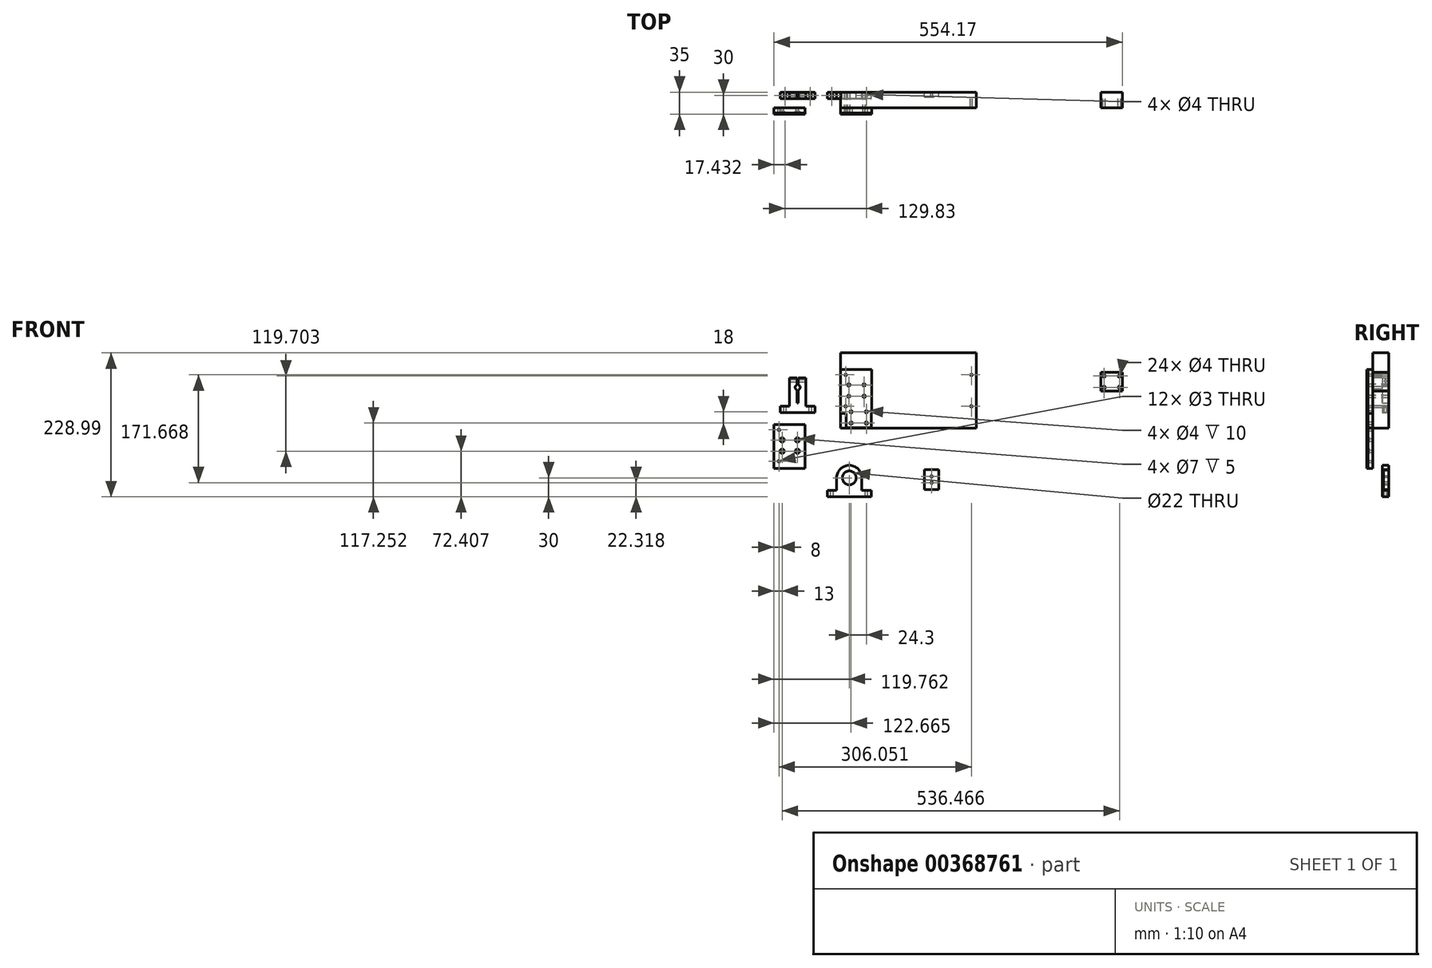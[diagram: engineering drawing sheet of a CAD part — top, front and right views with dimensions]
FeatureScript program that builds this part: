
annotation { "Feature Type Name" : "Feature", "Feature Type Description" : "" }
export const myFeature = defineFeature(function(context is Context, id is Id, definition is map)
    precondition{}
    {
        {
            var Q0;
            Q0=qCreatedBy(makeId("Front.planeOp"),FACE);
            var sketch = newSketch(context, id + "F0", { "sketchPlane" : qUnion([Q0])});
            skCircle(sketch, "E0", {"center": v(-230.1, -138.1) * mm, "radius": 11 * mm});
            skCircle(sketch, "E1", {"center": v(-230.1, -138.1) * mm, "radius": 4 * mm});
            skArc(sketch, "E2", {"start": v(-250.1, -138.1) * mm, "mid": v(-230.1, -118.1) * mm, "end": v(-210.1, -138.1) * mm});
            skLineSegment(sketch, "E3", {"start": v(-250.1, -138.1) * mm, "end": v(-250.1, -158.1) * mm});
            skLineSegment(sketch, "E4", {"start": v(-250.1, -158.1) * mm, "end": v(-265.1, -158.1) * mm});
            skLineSegment(sketch, "E5", {"start": v(-265.1, -158.1) * mm, "end": v(-265.1, -168.1) * mm});
            skLineSegment(sketch, "E6", {"start": v(-265.1, -168.1) * mm, "end": v(-195.1, -168.1) * mm});
            skLineSegment(sketch, "E7", {"start": v(-195.1, -168.1) * mm, "end": v(-195.1, -158.1) * mm});
            skLineSegment(sketch, "E8", {"start": v(-195.1, -158.1) * mm, "end": v(-210.1, -158.1) * mm});
            skLineSegment(sketch, "E9", {"start": v(-210.1, -158.1) * mm, "end": v(-210.1, -138.1) * mm});
            skLineSegment(sketch, "E10", {"start": v(-324.94, 21.01) * mm, "end": v(-324.94, -23.99) * mm});
            skLineSegment(sketch, "E11", {"start": v(-324.94, -23.99) * mm, "end": v(-339.94, -23.99) * mm});
            skLineSegment(sketch, "E12", {"start": v(-339.94, -23.99) * mm, "end": v(-339.94, -33.99) * mm});
            skLineSegment(sketch, "E13", {"start": v(-339.94, -33.99) * mm, "end": v(-284.44, -33.99) * mm});
            skLineSegment(sketch, "E14", {"start": v(-284.44, -33.99) * mm, "end": v(-284.44, -23.99) * mm});
            skLineSegment(sketch, "E15", {"start": v(-284.44, -23.99) * mm, "end": v(-299.44, -23.99) * mm});
            skLineSegment(sketch, "E16", {"start": v(-299.44, -23.99) * mm, "end": v(-299.44, 21.01) * mm});
            skPoint(sketch, "E17", {"position": v(-324.94, -1.49) * mm});
            skPoint(sketch, "E18", {"position": v(-312.19, -33.99) * mm});
            skLineSegment(sketch, "E19", {"start": v(-313.19, -18.99) * mm, "end": v(-311.19, -18.99) * mm});
            skLineSegment(sketch, "E20", {"start": v(-311.19, -18.99) * mm, "end": v(-311.19, 6.01) * mm});
            skLineSegment(sketch, "E21", {"start": v(-313.19, -18.99) * mm, "end": v(-313.19, 6.01) * mm});
            skPoint(sketch, "E22", {"position": v(-312.19, -18.99) * mm});
            skCircle(sketch, "E23", {"center": v(-312.19, 6.01) * mm, "radius": 4 * mm});
            skLineSegment(sketch, "E24", {"start": v(-324.94, 21.01) * mm, "end": v(-313.19, 21.01) * mm});
            skLineSegment(sketch, "E25", {"start": v(-313.19, 21.01) * mm, "end": v(-313.19, 6.01) * mm});
            skLineSegment(sketch, "E26", {"start": v(-311.19, 21.01) * mm, "end": v(-299.44, 21.01) * mm});
            skLineSegment(sketch, "E27", {"start": v(-311.19, 6.01) * mm, "end": v(-311.19, 21.01) * mm});
            skLineSegment(sketch, "E28.bottom", {"start": v(-110.58, -124.8) * mm, "end": v(-87.58, -124.8) * mm});
            skLineSegment(sketch, "E28.top", {"start": v(-110.58, -156.8) * mm, "end": v(-87.58, -156.8) * mm});
            skLineSegment(sketch, "E28.left", {"start": v(-110.58, -124.8) * mm, "end": v(-110.58, -156.8) * mm});
            skLineSegment(sketch, "E28.right", {"start": v(-87.58, -124.8) * mm, "end": v(-87.58, -156.8) * mm});
            skPoint(sketch, "E29", {"position": v(-99.08, -124.8) * mm});
            skCircle(sketch, "E30", {"center": v(-99.08, -135.8) * mm, "radius": 1.5 * mm});
            skCircle(sketch, "E31", {"center": v(-99.08, -145.8) * mm, "radius": 1.5 * mm});
            skSolve(sketch);
        }
        {
            var Q0;
            Q0=makeQuery(id+"F0.imprint","IMPRINT",FACE,{"disambiguationData":[TD([[makeQuery(id+"F0.imprint","IMPRINT",EDGE,{"derivedFrom":sQuery(id+"F0.wireOp",EDGE,"E0")}),-1.0]])]});
            extrude(context, id + "F1", {"entities" : qUnion([Q0]), "depth" : 10 * mm, "offsetDistance" : 25 * mm});
        }
        {
            var Q0;
            Q0=makeQuery(id+"F1.opExtrude","SWEPT_FACE",FACE,{"disambiguationData":[OSD([sQuery(id+"F0.wireOp",EDGE,"E4")])]});
            var sketch = newSketch(context, id + "F2", { "sketchPlane" : qUnion([Q0])});
            skCircle(sketch, "E32", {"center": v(-257.6, -5) * mm, "radius": 2 * mm});
            skCircle(sketch, "E33", {"center": v(-202.6, -5) * mm, "radius": 2 * mm});
            skPoint(sketch, "E33.centerSnap0", {"position": v(-250.1, -5) * mm});
            skPoint(sketch, "E34", {"position": v(-265.1, -5) * mm});
            skSolve(sketch);
        }
        {
            var Q0;
            Q0 = qSketchRegion(id + "F2", true);
            extrude(context, id + "F3", {"entities" : qUnion([Q0]), "operationType" : NewBodyOperationType.REMOVE, "oppositeDirection" : true, "depth" : 25 * mm, "offsetDistance" : 25 * mm});
        }
        {
            var Q0;
            Q0=makeQuery(id+"F0.imprint","IMPRINT",FACE,{"disambiguationData":[TD([[makeQuery(id+"F0.imprint","IMPRINT",EDGE,{"derivedFrom":sQuery(id+"F0.wireOp",EDGE,"E10")}),1.0]])]});
            extrude(context, id + "F4", {"entities" : qUnion([Q0]), "depth" : 10 * mm, "offsetDistance" : 25 * mm});
        }
        {
            var Q0;
            Q0=makeQuery(id+"F4.opExtrude","SWEPT_FACE",FACE,{"disambiguationData":[OSD([sQuery(id+"F0.wireOp",EDGE,"E10")])]});
            var sketch = newSketch(context, id + "F5", { "sketchPlane" : qUnion([Q0])});
            skCircle(sketch, "E35", {"center": v(4.76, 16.01) * mm, "radius": 2 * mm});
            skSolve(sketch);
        }
        {
            var Q0;
            Q0=makeQuery(id+"F5.imprint","IMPRINT",FACE,{"disambiguationData":[TD([[makeQuery(id+"F5.imprint","IMPRINT",EDGE,{"derivedFrom":sQuery(id+"F5.wireOp",EDGE,"E35")}),1.0]])]});
            extrude(context, id + "F6", {"entities" : qUnion([Q0]), "operationType" : NewBodyOperationType.REMOVE, "oppositeDirection" : true, "depth" : 36.2 * mm, "offsetDistance" : 25 * mm});
        }
        {
            var Q0;
            Q0=makeQuery(id+"F4.opExtrude","SWEPT_FACE",FACE,{"disambiguationData":[OSD([sQuery(id+"F0.wireOp",EDGE,"E11")])]});
            var sketch = newSketch(context, id + "F7", { "sketchPlane" : qUnion([Q0])});
            skCircle(sketch, "E36", {"center": v(-332.44, -5) * mm, "radius": 2 * mm});
            skPoint(sketch, "E37", {"position": v(-332.44, 0) * mm});
            skPoint(sketch, "E38", {"position": v(-339.94, -5) * mm});
            skSolve(sketch);
        }
        {
            var Q0;
            Q0=makeQuery(id+"F4.opExtrude","SWEPT_FACE",FACE,{"disambiguationData":[OSD([sQuery(id+"F0.wireOp",EDGE,"E15")])]});
            var sketch = newSketch(context, id + "F8", { "sketchPlane" : qUnion([Q0])});
            skPoint(sketch, "E39", {"position": v(-291.94, 0) * mm});
            skPoint(sketch, "E40", {"position": v(-284.44, -5) * mm});
            skCircle(sketch, "E41", {"center": v(-291.94, -5) * mm, "radius": 2 * mm});
            skSolve(sketch);
        }
        {
            var Q0;
            Q0=makeQuery(id+"F8.imprint","IMPRINT",FACE,{"disambiguationData":[TD([[makeQuery(id+"F8.imprint","IMPRINT",EDGE,{"derivedFrom":sQuery(id+"F8.wireOp",EDGE,"E41")}),1.0]])]});
            var Q1;
            Q1=makeQuery(id+"F7.imprint","IMPRINT",FACE,{"disambiguationData":[TD([[makeQuery(id+"F7.imprint","IMPRINT",EDGE,{"derivedFrom":sQuery(id+"F7.wireOp",EDGE,"E36")}),1.0]])]});
            var Q2;
            Q2 = qSketchRegion(id + "F10", true);
            extrude(context, id + "F9", {"entities" : qUnion([Q0, Q1, Q2]), "operationType" : NewBodyOperationType.REMOVE, "oppositeDirection" : true, "depth" : 25 * mm, "offsetDistance" : 25 * mm});
        }
        {
            var Q0;
            Q0=qCreatedBy(makeId("Front.planeOp"),FACE);
            var sketch = newSketch(context, id + "F10", { "sketchPlane" : qUnion([Q0])});
            skLineSegment(sketch, "E42.bottom", {"start": v(-243.82, 60.88) * mm, "end": v(-27.82, 60.88) * mm});
            skLineSegment(sketch, "E42.top", {"start": v(-243.82, -59.12) * mm, "end": v(-27.82, -59.12) * mm});
            skLineSegment(sketch, "E42.left", {"start": v(-243.82, 60.88) * mm, "end": v(-243.82, -59.12) * mm});
            skLineSegment(sketch, "E42.right", {"start": v(-27.82, 60.88) * mm, "end": v(-27.82, -59.12) * mm});
            skLineSegment(sketch, "E43", {"start": v(-235.82, 75.54) * mm, "end": v(-235.82, -77.95) * mm, "construction": true});
            skLineSegment(sketch, "E44", {"start": v(-35.82, 74.3) * mm, "end": v(-35.82, -77.95) * mm, "construction": true});
            skLineSegment(sketch, "E45", {"start": v(-230.82, 76.77) * mm, "end": v(-230.82, -80.82) * mm, "construction": true});
            skLineSegment(sketch, "E46", {"start": v(-40.82, 75.13) * mm, "end": v(-40.82, -75.08) * mm, "construction": true});
            skLineSegment(sketch, "E47", {"start": v(-274.06, -24.12) * mm, "end": v(20.6, -24.12) * mm, "construction": true});
            skLineSegment(sketch, "E48", {"start": v(-271.18, 25.88) * mm, "end": v(19.79, 25.88) * mm, "construction": true});
            skCircle(sketch, "E49", {"center": v(-235.82, 25.88) * mm, "radius": 1.5 * mm});
            skCircle(sketch, "E50", {"center": v(-235.82, -24.12) * mm, "radius": 1.5 * mm});
            skCircle(sketch, "E51", {"center": v(-35.82, 25.88) * mm, "radius": 1.5 * mm});
            skCircle(sketch, "E52", {"center": v(-35.82, -24.12) * mm, "radius": 1.5 * mm});
            skCircle(sketch, "E53", {"center": v(175.3, 24) * mm, "radius": 2 * mm});
            skCircle(sketch, "E54", {"center": v(175.3, 6) * mm, "radius": 2 * mm});
            skLineSegment(sketch, "E55.bottom", {"start": v(170.3, 30) * mm, "end": v(204.3, 30) * mm});
            skLineSegment(sketch, "E55.top", {"start": v(170.3, 0) * mm, "end": v(204.3, 0) * mm});
            skLineSegment(sketch, "E55.left", {"start": v(170.3, 30) * mm, "end": v(170.3, 0) * mm});
            skLineSegment(sketch, "E55.right", {"start": v(204.3, 30) * mm, "end": v(204.3, 0) * mm});
            skLineSegment(sketch, "E56", {"start": v(180.3, 30) * mm, "end": v(180.3, 0) * mm});
            skLineSegment(sketch, "E57", {"start": v(194.3, 30) * mm, "end": v(194.3, 0) * mm});
            skCircle(sketch, "E58", {"center": v(199.6, 24) * mm, "radius": 2 * mm});
            skCircle(sketch, "E59", {"center": v(199.6, 6) * mm, "radius": 2 * mm});
            skPoint(sketch, "E60", {"position": v(-243.82, 0.88) * mm});
            skPoint(sketch, "E61", {"position": v(170.3, 15) * mm});
            skCircle(sketch, "E62", {"center": v(-230.82, 9.88) * mm, "radius": 2 * mm});
            skCircle(sketch, "E63", {"center": v(-230.82, -8.12) * mm, "radius": 2 * mm});
            skLineSegment(sketch, "E64.bottom", {"start": v(-235.82, 15.88) * mm, "end": v(-201.82, 15.88) * mm});
            skLineSegment(sketch, "E64.top", {"start": v(-235.82, -14.12) * mm, "end": v(-201.82, -14.12) * mm});
            skLineSegment(sketch, "E64.left", {"start": v(-235.82, 15.88) * mm, "end": v(-235.82, -14.12) * mm});
            skLineSegment(sketch, "E64.right", {"start": v(-201.82, 15.88) * mm, "end": v(-201.82, -14.12) * mm});
            skLineSegment(sketch, "E65", {"start": v(-225.82, 15.88) * mm, "end": v(-225.82, -14.12) * mm});
            skLineSegment(sketch, "E66", {"start": v(-211.82, 15.88) * mm, "end": v(-211.82, -14.12) * mm});
            skCircle(sketch, "E67", {"center": v(-206.52, 9.88) * mm, "radius": 2 * mm});
            skCircle(sketch, "E68", {"center": v(-206.52, -8.12) * mm, "radius": 2 * mm});
            skPoint(sketch, "E69", {"position": v(-235.82, 0.88) * mm});
            skSolve(sketch);
        }
        {
            var Q0;
            Q0=makeQuery(id+"F10.imprint","IMPRINT",FACE,{"disambiguationData":[TD([[makeQuery(id+"F10.imprint","IMPRINT",EDGE,{"derivedFrom":sQuery(id+"F10.wireOp",EDGE,"E53")}),-1.0]])]});
            var Q1;
            {var subQ1=sQuery(id+"F10.wireOp",EDGE,"E55.right");Q1=makeQuery(id+"F10.imprint","IMPRINT",FACE,{"disambiguationData":[TD([[makeQuery(id+"F10.imprint","IMPRINT",EDGE,{"derivedFrom":subQ1}),-1.0]])]});}
            var Q2;
            Q2=makeQuery(id+"F10.imprint","IMPRINT",FACE,{"disambiguationData":[TD([[makeQuery(id+"F10.imprint","IMPRINT",EDGE,{"derivedFrom":sQuery(id+"F10.wireOp",EDGE,"E42.bottom")}),-1.0]])]});
            var Q3;
            {var subQ0=sQuery(id+"F10.wireOp",EDGE,"E56");Q3=makeQuery(id+"F10.imprint","IMPRINT",FACE,{"disambiguationData":[TD([[makeQuery(id+"F10.imprint","IMPRINT",EDGE,{"derivedFrom":subQ0}),1.0]])]});}
            var Q4;
            Q4=makeQuery(id+"F10.imprint","IMPRINT",FACE,{"disambiguationData":[TD([[makeQuery(id+"F10.imprint","IMPRINT",EDGE,{"derivedFrom":sQuery(id+"F10.wireOp",EDGE,"E62")}),-1.0]])]});
            var Q5;
            {var subQ0=sQuery(id+"F10.wireOp",EDGE,"E65");Q5=makeQuery(id+"F10.imprint","IMPRINT",FACE,{"disambiguationData":[TD([[makeQuery(id+"F10.imprint","IMPRINT",EDGE,{"derivedFrom":subQ0}),1.0]])]});}
            var Q6;
            {var subQ1=sQuery(id+"F10.wireOp",EDGE,"E64.right");Q6=makeQuery(id+"F10.imprint","IMPRINT",FACE,{"disambiguationData":[TD([[makeQuery(id+"F10.imprint","IMPRINT",EDGE,{"derivedFrom":subQ1}),-1.0]])]});}
            extrude(context, id + "F11", {"entities" : qUnion([Q0, Q1, Q2, Q3, Q4, Q5, Q6]), "depth" : 25 * mm, "offsetDistance" : 25 * mm});
        }
        {
            var Q0;
            Q0=makeQuery(id+"F11.opExtrude","CAP_FACE",FACE,{"disambiguationData":[OSD([sQuery(id+"F10.wireOp",EDGE,"E42.bottom"),sQuery(id+"F10.wireOp",EDGE,"E42.top"),sQuery(id+"F10.wireOp",EDGE,"E42.left"),sQuery(id+"F10.wireOp",EDGE,"E42.right"),sQuery(id+"F10.wireOp",EDGE,"E49"),sQuery(id+"F10.wireOp",EDGE,"E50"),sQuery(id+"F10.wireOp",EDGE,"E51"),sQuery(id+"F10.wireOp",EDGE,"E52"),sQuery(id+"F10.wireOp",EDGE,"E62"),sQuery(id+"F10.wireOp",EDGE,"E63"),sQuery(id+"F10.wireOp",EDGE,"E67"),sQuery(id+"F10.wireOp",EDGE,"E68")])],"isStart":false});
            var sketch = newSketch(context, id + "F12", { "sketchPlane" : qUnion([Q0])});
            skLineSegment(sketch, "E70.bottom", {"start": v(-194.52, 34.38) * mm, "end": v(-243.82, 34.38) * mm});
            skLineSegment(sketch, "E70.top", {"start": v(-194.52, -35.62) * mm, "end": v(-243.82, -35.62) * mm});
            skLineSegment(sketch, "E70.left", {"start": v(-194.52, 34.38) * mm, "end": v(-194.52, -35.62) * mm});
            skLineSegment(sketch, "E70.right", {"start": v(-243.82, 34.38) * mm, "end": v(-243.82, -35.62) * mm});
            skCircle(sketch, "E71", {"center": v(-206.52, 9.88) * mm, "radius": 2 * mm});
            skCircle(sketch, "E72", {"center": v(-206.52, -8.12) * mm, "radius": 2 * mm});
            skCircle(sketch, "E73", {"center": v(-230.82, -8.12) * mm, "radius": 2 * mm});
            skCircle(sketch, "E74", {"center": v(-230.82, 9.88) * mm, "radius": 2 * mm});
            skCircle(sketch, "E75", {"center": v(-235.82, 25.88) * mm, "radius": 1.5 * mm});
            skCircle(sketch, "E76", {"center": v(-235.82, -24.12) * mm, "radius": 1.5 * mm});
            skLineSegment(sketch, "E77.bottom", {"start": v(-300.57, -53.2) * mm, "end": v(-349.87, -53.2) * mm});
            skLineSegment(sketch, "E77.top", {"start": v(-300.57, -123.2) * mm, "end": v(-349.87, -123.2) * mm});
            skLineSegment(sketch, "E77.left", {"start": v(-300.57, -53.2) * mm, "end": v(-300.57, -123.2) * mm});
            skLineSegment(sketch, "E77.right", {"start": v(-349.87, -53.2) * mm, "end": v(-349.87, -123.2) * mm});
            skCircle(sketch, "E78", {"center": v(-312.57, -77.7) * mm, "radius": 2 * mm});
            skCircle(sketch, "E79", {"center": v(-312.57, -95.7) * mm, "radius": 2 * mm});
            skCircle(sketch, "E80", {"center": v(-336.87, -95.7) * mm, "radius": 2 * mm});
            skCircle(sketch, "E81", {"center": v(-336.87, -77.7) * mm, "radius": 2 * mm});
            skCircle(sketch, "E82", {"center": v(-341.87, -61.7) * mm, "radius": 1.5 * mm});
            skCircle(sketch, "E83", {"center": v(-341.87, -111.7) * mm, "radius": 1.5 * mm});
            skLineSegment(sketch, "E84.bottom", {"start": v(-235.24, -25.22) * mm, "end": v(-195.02, -25.22) * mm});
            skLineSegment(sketch, "E84.top", {"start": v(-235.24, -58.08) * mm, "end": v(-195.02, -58.08) * mm});
            skLineSegment(sketch, "E84.left", {"start": v(-235.24, -25.22) * mm, "end": v(-235.24, -58.08) * mm});
            skLineSegment(sketch, "E84.right", {"start": v(-195.02, -25.22) * mm, "end": v(-195.02, -58.08) * mm});
            skCircle(sketch, "E85", {"center": v(-202.9, -32.86) * mm, "radius": 2 * mm});
            skCircle(sketch, "E86", {"center": v(-202.9, -50.86) * mm, "radius": 2 * mm});
            skCircle(sketch, "E87", {"center": v(-227.2, -50.86) * mm, "radius": 2 * mm});
            skCircle(sketch, "E88", {"center": v(-227.2, -32.86) * mm, "radius": 2 * mm});
            skSolve(sketch);
        }
        {
            var Q0;
            Q0 = qSketchRegion(id + "F12", true);
            extrude(context, id + "F13", {"entities" : qUnion([Q0]), "operationType" : NewBodyOperationType.ADD, "depth" : 10 * mm, "offsetDistance" : 25 * mm});
        }
        {
            var Q0;
            Q0=makeQuery(id+"F13.opExtrude","CAP_FACE",FACE,{"disambiguationData":[OSD([sQuery(id+"F12.wireOp",EDGE,"E77.bottom"),sQuery(id+"F12.wireOp",EDGE,"E77.top"),sQuery(id+"F12.wireOp",EDGE,"E77.left"),sQuery(id+"F12.wireOp",EDGE,"E77.right"),sQuery(id+"F12.wireOp",EDGE,"E78"),sQuery(id+"F12.wireOp",EDGE,"E79"),sQuery(id+"F12.wireOp",EDGE,"E80"),sQuery(id+"F12.wireOp",EDGE,"E81"),sQuery(id+"F12.wireOp",EDGE,"E82"),sQuery(id+"F12.wireOp",EDGE,"E83")])],"isStart":false});
            var sketch = newSketch(context, id + "F14", { "sketchPlane" : qUnion([Q0])});
            skCircle(sketch, "E89", {"center": v(-336.87, -77.7) * mm, "radius": 3.5 * mm});
            skCircle(sketch, "E90", {"center": v(-312.57, -77.7) * mm, "radius": 3.5 * mm});
            skCircle(sketch, "E91", {"center": v(-336.87, -95.7) * mm, "radius": 3.5 * mm});
            skCircle(sketch, "E92", {"center": v(-312.57, -95.7) * mm, "radius": 3.5 * mm});
            skSolve(sketch);
        }
        {
            var Q0;
            Q0 = qSketchRegion(id + "F14", true);
            extrude(context, id + "F15", {"entities" : qUnion([Q0]), "operationType" : NewBodyOperationType.REMOVE, "oppositeDirection" : true, "depth" : 5 * mm, "offsetDistance" : 25 * mm});
        }
        {
            var Q0;
            Q0=makeQuery(id+"F0.imprint","IMPRINT",FACE,{"disambiguationData":[TD([[makeQuery(id+"F0.imprint","IMPRINT",EDGE,{"derivedFrom":sQuery(id+"F0.wireOp",EDGE,"E28.bottom")}),-1.0]])]});
            var Q1;
            Q1 = qSketchRegion(id + "F12", true);
            extrude(context, id + "F16", {"entities" : qUnion([Q0, Q1]), "depth" : 8 * mm, "offsetDistance" : 25 * mm});
        }
    });
